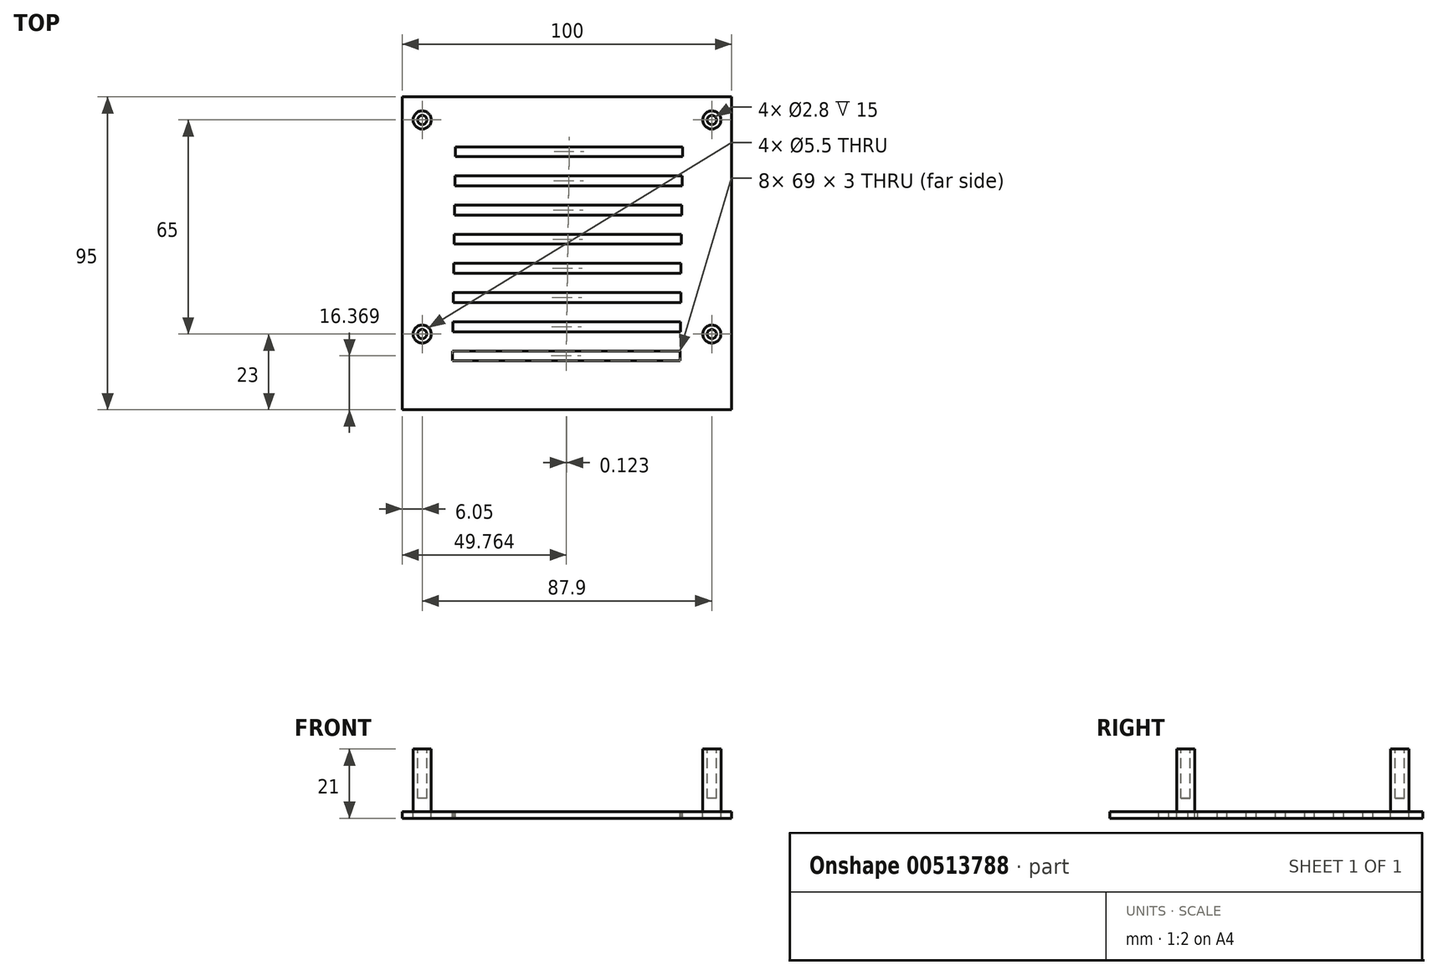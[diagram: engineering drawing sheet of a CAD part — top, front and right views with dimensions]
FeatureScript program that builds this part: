
annotation { "Feature Type Name" : "Feature", "Feature Type Description" : "" }
export const myFeature = defineFeature(function(context is Context, id is Id, definition is map)
    precondition{}
    {
        {
            var Q0;
            Q0=qCreatedBy(makeId("Top.planeOp"),FACE);
            var sketch = newSketch(context, id + "F0", { "sketchPlane" : qUnion([Q0])});
            skLineSegment(sketch, "E0.bottom", {"start": v(0, 0) * mm, "end": v(100, 0) * mm});
            skLineSegment(sketch, "E0.top", {"start": v(0, 95) * mm, "end": v(100, 95) * mm});
            skLineSegment(sketch, "E0.left", {"start": v(0, 0) * mm, "end": v(0, 95) * mm});
            skLineSegment(sketch, "E0.right", {"start": v(100, 0) * mm, "end": v(100, 95) * mm});
            skCircle(sketch, "E1", {"center": v(6.05, 88) * mm, "radius": 2.75 * mm});
            skCircle(sketch, "E2", {"center": v(93.95, 88) * mm, "radius": 2.75 * mm});
            skCircle(sketch, "E3", {"center": v(6.05, 23) * mm, "radius": 2.75 * mm});
            skCircle(sketch, "E4", {"center": v(93.95, 23) * mm, "radius": 2.75 * mm});
            skLineSegment(sketch, "E5.bottom", {"start": v(16.12, 79.86) * mm, "end": v(85.12, 79.86) * mm});
            skLineSegment(sketch, "E5.top", {"start": v(16.12, 76.86) * mm, "end": v(85.12, 76.86) * mm});
            skLineSegment(sketch, "E5.left", {"start": v(16.12, 79.86) * mm, "end": v(16.12, 76.86) * mm});
            skLineSegment(sketch, "E5.right", {"start": v(85.12, 79.86) * mm, "end": v(85.12, 76.86) * mm});
            skLineSegment(sketch, "E6.1.0.0", {"start": v(16, 71) * mm, "end": v(85, 71) * mm});
            skLineSegment(sketch, "E6.1.0.1", {"start": v(16, 68) * mm, "end": v(85, 68) * mm});
            skLineSegment(sketch, "E6.1.0.2", {"start": v(16, 71) * mm, "end": v(16, 68) * mm});
            skLineSegment(sketch, "E6.1.0.3", {"start": v(85, 71) * mm, "end": v(85, 68) * mm});
            skLineSegment(sketch, "E6.2.0.0", {"start": v(15.88, 62.14) * mm, "end": v(84.88, 62.14) * mm});
            skLineSegment(sketch, "E6.2.0.1", {"start": v(15.88, 59.14) * mm, "end": v(84.88, 59.14) * mm});
            skLineSegment(sketch, "E6.2.0.2", {"start": v(15.88, 62.14) * mm, "end": v(15.88, 59.14) * mm});
            skLineSegment(sketch, "E6.2.0.3", {"start": v(84.88, 62.14) * mm, "end": v(84.88, 59.14) * mm});
            skLineSegment(sketch, "E6.3.0.0", {"start": v(15.75, 53.29) * mm, "end": v(84.75, 53.29) * mm});
            skLineSegment(sketch, "E6.3.0.1", {"start": v(15.75, 50.29) * mm, "end": v(84.75, 50.29) * mm});
            skLineSegment(sketch, "E6.3.0.2", {"start": v(15.75, 53.29) * mm, "end": v(15.75, 50.29) * mm});
            skLineSegment(sketch, "E6.3.0.3", {"start": v(84.75, 53.29) * mm, "end": v(84.75, 50.29) * mm});
            skLineSegment(sketch, "E6.4.0.0", {"start": v(15.63, 44.43) * mm, "end": v(84.63, 44.43) * mm});
            skLineSegment(sketch, "E6.4.0.1", {"start": v(15.63, 41.43) * mm, "end": v(84.63, 41.43) * mm});
            skLineSegment(sketch, "E6.4.0.2", {"start": v(15.63, 44.43) * mm, "end": v(15.63, 41.43) * mm});
            skLineSegment(sketch, "E6.4.0.3", {"start": v(84.63, 44.43) * mm, "end": v(84.63, 41.43) * mm});
            skLineSegment(sketch, "E6.5.0.0", {"start": v(15.5, 35.58) * mm, "end": v(84.5, 35.58) * mm});
            skLineSegment(sketch, "E6.5.0.1", {"start": v(15.5, 32.58) * mm, "end": v(84.5, 32.58) * mm});
            skLineSegment(sketch, "E6.5.0.2", {"start": v(15.5, 35.58) * mm, "end": v(15.5, 32.58) * mm});
            skLineSegment(sketch, "E6.5.0.3", {"start": v(84.5, 35.58) * mm, "end": v(84.5, 32.58) * mm});
            skLineSegment(sketch, "E6.6.0.0", {"start": v(15.39, 26.72) * mm, "end": v(84.39, 26.72) * mm});
            skLineSegment(sketch, "E6.6.0.1", {"start": v(15.39, 23.72) * mm, "end": v(84.39, 23.72) * mm});
            skLineSegment(sketch, "E6.6.0.2", {"start": v(15.39, 26.72) * mm, "end": v(15.39, 23.72) * mm});
            skLineSegment(sketch, "E6.6.0.3", {"start": v(84.39, 26.72) * mm, "end": v(84.39, 23.72) * mm});
            skLineSegment(sketch, "E6.7.0.0", {"start": v(15.26, 17.87) * mm, "end": v(84.26, 17.87) * mm});
            skLineSegment(sketch, "E6.7.0.1", {"start": v(15.26, 14.87) * mm, "end": v(84.26, 14.87) * mm});
            skLineSegment(sketch, "E6.7.0.2", {"start": v(15.26, 17.87) * mm, "end": v(15.26, 14.87) * mm});
            skLineSegment(sketch, "E6.7.0.3", {"start": v(84.26, 17.87) * mm, "end": v(84.26, 14.87) * mm});
            skLineSegment(sketch, "E6.direction1", {"start": v(16.12, 79.86) * mm, "end": v(16, 71) * mm, "construction": true});
            skSolve(sketch);
        }
        {
            var Q0;
            Q0=makeQuery(id+"F0.imprint","IMPRINT",FACE,{"disambiguationData":[TD([[makeQuery(id+"F0.imprint","IMPRINT",EDGE,{"derivedFrom":sQuery(id+"F0.wireOp",EDGE,"E0.bottom")}),1.0]])]});
            extrude(context, id + "F1", {"entities" : qUnion([Q0]), "oppositeDirection" : true, "depth" : 2 * mm});
        }
        {
            var Q0;
            Q0=makeQuery(id+"F0.imprint","IMPRINT",FACE,{"disambiguationData":[TD([[makeQuery(id+"F0.imprint","IMPRINT",EDGE,{"derivedFrom":sQuery(id+"F0.wireOp",EDGE,"E1")}),1.0]])]});
            var Q1;
            Q1=makeQuery(id+"F0.imprint","IMPRINT",FACE,{"disambiguationData":[TD([[makeQuery(id+"F0.imprint","IMPRINT",EDGE,{"derivedFrom":sQuery(id+"F0.wireOp",EDGE,"E2")}),1.0]])]});
            var Q2;
            Q2=makeQuery(id+"F0.imprint","IMPRINT",FACE,{"disambiguationData":[TD([[makeQuery(id+"F0.imprint","IMPRINT",EDGE,{"derivedFrom":sQuery(id+"F0.wireOp",EDGE,"E4")}),1.0]])]});
            var Q3;
            Q3=makeQuery(id+"F0.imprint","IMPRINT",FACE,{"disambiguationData":[TD([[makeQuery(id+"F0.imprint","IMPRINT",EDGE,{"derivedFrom":sQuery(id+"F0.wireOp",EDGE,"E3")}),1.0]])]});
            extrude(context, id + "F2", {"entities" : qUnion([Q0, Q1, Q2, Q3]), "depth" : 19 * mm});
        }
        {
            var Q0;
            Q0=makeQuery(id+"F2.opExtrude","CAP_FACE",FACE,{"disambiguationData":[OSD([sQuery(id+"F0.wireOp",EDGE,"E1")])],"isStart":false});
            var sketch = newSketch(context, id + "F3", { "sketchPlane" : qUnion([Q0])});
            skCircle(sketch, "E7", {"center": v(6.05, 88) * mm, "radius": 1.4 * mm});
            skCircle(sketch, "E8", {"center": v(93.95, 88) * mm, "radius": 1.4 * mm});
            skCircle(sketch, "E9", {"center": v(6.05, 23) * mm, "radius": 1.4 * mm});
            skCircle(sketch, "E10", {"center": v(93.95, 23) * mm, "radius": 1.4 * mm});
            skSolve(sketch);
        }
        {
            var Q0;
            Q0=makeQuery(id+"F3.imprint","IMPRINT",FACE,{"disambiguationData":[TD([[makeQuery(id+"F3.imprint","IMPRINT",EDGE,{"derivedFrom":sQuery(id+"F3.wireOp",EDGE,"E7")}),1.0]])]});
            var Q1;
            Q1=makeQuery(id+"F3.imprint","IMPRINT",FACE,{"disambiguationData":[TD([[makeQuery(id+"F3.imprint","IMPRINT",EDGE,{"derivedFrom":sQuery(id+"F3.wireOp",EDGE,"E8")}),1.0]])]});
            var Q2;
            Q2=makeQuery(id+"F3.imprint","IMPRINT",FACE,{"disambiguationData":[TD([[makeQuery(id+"F3.imprint","IMPRINT",EDGE,{"derivedFrom":sQuery(id+"F3.wireOp",EDGE,"E9")}),1.0]])]});
            var Q3;
            Q3=makeQuery(id+"F3.imprint","IMPRINT",FACE,{"disambiguationData":[TD([[makeQuery(id+"F3.imprint","IMPRINT",EDGE,{"derivedFrom":sQuery(id+"F3.wireOp",EDGE,"E10")}),1.0]])]});
            extrude(context, id + "F4", {"entities" : qUnion([Q0, Q1, Q2, Q3]), "operationType" : NewBodyOperationType.REMOVE, "oppositeDirection" : true, "depth" : 15 * mm});
        }
    });
